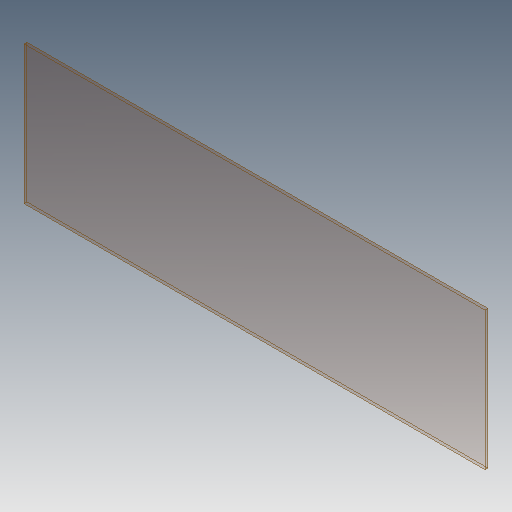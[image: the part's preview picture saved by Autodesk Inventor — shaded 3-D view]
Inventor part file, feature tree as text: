
AUTODESK INVENTOR PART (.ipt)
format: ipt  version: 2018 (Build 220112000, 112)  size: 87,552 bytes
history: native  units: mm
features: other x1, extrude x1, sketch x1
ambient origin geometry x8: Origin, YZ Plane, XZ Plane, XY Plane, X Axis, Y Axis, Z Axis, Center Point
bodies: Solid1 (feature_tree)
feature tree (3):
  other  "<userpath>\OneDrive\projects\sPhenixTileTestStand\sPhenixTileTestStand.xlsx"
  extrude  "Extrusion1"  Depth=150.0mm
  sketch  "Sketch2"  dims[d1=500.0mm d2=150.0mm d3=3.125mm d4=0.0mm]
